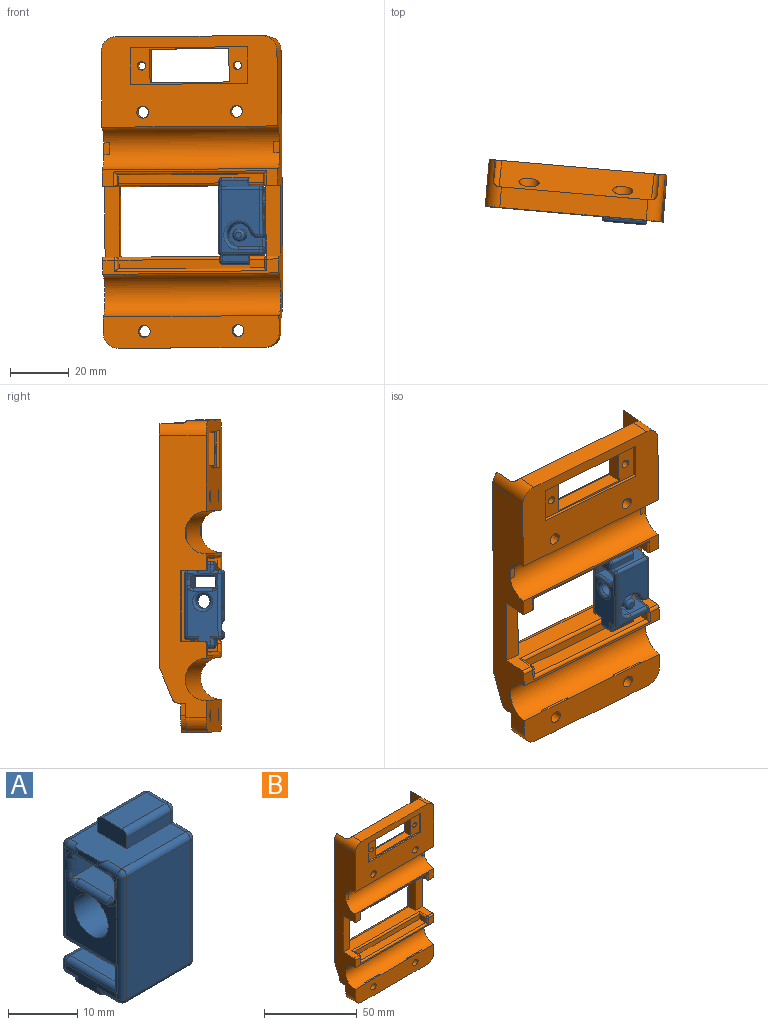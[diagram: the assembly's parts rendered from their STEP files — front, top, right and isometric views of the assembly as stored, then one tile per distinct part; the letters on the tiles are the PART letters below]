
ASSEMBLY  parts=2 mates=1
PART A: 97 faces, bbox 15.1x12.6x29.6 mm
  f0: cylinder r=2.45mm len=9mm, axis (1,0,0), area 131.3mm2, adj f77,f94,f95
  f1: plane 10.5x1.92mm, normal (-1,0,0), area 13.7mm2, adj f2,f24,f39,f40,f42,f43,f44,f92
  f2: cylinder r=1mm len=1mm, axis (0,0,-1), area 1.5mm2, adj f1,f25,f38,f91
  f3: torus R=2mm, axis (-1,0,0), area 2.6mm2, adj f8,f36,f43,f67,f68
  f4: torus R=2mm, axis (-1,0,0), area 2.6mm2, adj f7,f36,f37,f67,f70
  f5: torus R=2mm, axis (-1,0,0), area 2.6mm2, adj f12,f48,f63,f67,f68
  f6: torus R=2mm, axis (-1,0,0), area 2.6mm2, adj f11,f47,f48,f67,f70
  f7: plane 2x2mm, normal (-1,0,0), area 0.9mm2, adj f4,f36,f37
  f8: plane 2x2mm, normal (-1,0,0), area 0.9mm2, adj f3,f36,f43
  f9: plane 11.58x10.5mm, normal (-1,0,0), area 64.9mm2, adj f37,f43,f71,f72,f73,f88,f96
  f10: plane 20.5x10.5mm, normal (1,0,0), area 139.1mm2, adj f47,f51,f53,f57,f60,f62,f63,f74
  f11: plane 2x2mm, normal (1,0,0), area 0.9mm2, adj f6,f47,f48
  f12: plane 2x2mm, normal (1,0,0), area 0.9mm2, adj f5,f48,f63
  f13: plane 4x1mm, normal (-1,0,0), area 4mm2, adj f21,f22,f28,f36
  f14: plane 4x3mm, normal (1,0,0), area 12mm2, adj f48,f50,f54,f58
  f15: plane 9x2mm, normal (0,1,0), area 18mm2, adj f20,f24,f53,f65
  f16: plane 9x2mm, normal (0,1,0), area 18mm2, adj f28,f32,f50,f66
  f17: plane 9x2mm, normal (0,-1,0), area 18mm2, adj f19,f24,f60,f65
  f18: plane 9x4mm, normal (0,0,-1), area 36mm2, adj f19,f20,f57,f65
  f19: cylinder r=1mm len=9mm, axis (-1,0,0), area 14.1mm2, adj f17,f18,f59,f65
  f20: cylinder r=1mm len=9mm, axis (1,0,0), area 14.1mm2, adj f15,f18,f55,f65
  f21: cylinder r=1mm len=1mm, axis (0,0,-1), area 0.6mm2, adj f13,f28,f36
  f22: cylinder r=1mm len=1mm, axis (0,0,1), area 0.6mm2, adj f13,f28,f36
  f23: plane 21.5x13mm, normal (0,-1,0), area 279.5mm2, adj f29,f34,f43,f63
  f24: plane 14x10.5mm, normal (0,0,-1), area 88.1mm2, adj f1,f15,f17,f29,f30,f39,f40,f42
  f25: plane 21.5x13mm, normal (0,1,0), area 183.9mm2, adj f2,f30,f31,f37,f47,f84,f85,f87
  f26: plane 9x4mm, normal (0,0,1), area 36mm2, adj f32,f33,f54,f66
  f27: plane 9x2mm, normal (0,-1,0), area 18mm2, adj f28,f33,f58,f66
  f28: plane 14x10.5mm, normal (0,0,1), area 88.1mm2, adj f13,f16,f21,f22,f27,f31,f34,f36
  f29: cylinder r=1mm len=13mm, axis (1,0,0), area 20.4mm2, adj f23,f24,f45,f64
  f30: cylinder r=1mm len=13mm, axis (-1,0,0), area 20.4mm2, adj f24,f25,f38,f49
  f31: cylinder r=1mm len=13mm, axis (1,0,0), area 20.4mm2, adj f25,f28,f35,f46
  f32: cylinder r=1mm len=9mm, axis (1,0,0), area 14.1mm2, adj f16,f26,f52,f66
  f33: cylinder r=1mm len=9mm, axis (-1,0,0), area 14.1mm2, adj f26,f27,f56,f66
  f34: cylinder r=1mm len=13mm, axis (-1,0,0), area 20.4mm2, adj f23,f28,f41,f61
  f35: sphere r=1mm, area 1.6mm2, adj f31,f36,f37
  f36: cylinder r=1mm len=10.5mm, axis (0,1,0), area 18.4mm2, adj f3,f4,f7,f8,f13,f21,f22,f28
  f37: cylinder r=1mm len=15.58mm, axis (0,0,-1), area 27.6mm2, adj f4,f7,f9,f25,f35,f70,f73,f86
  f38: sphere r=1mm, area 1.6mm2, adj f2,f30,f39
  f39: cylinder r=1mm len=2.5mm, axis (0,-1,0), area 2.9mm2, adj f1,f24,f38,f40
  f40: cylinder r=1mm len=1mm, axis (0,0,-1), area 0.6mm2, adj f1,f24,f39
  f41: sphere r=1mm, area 1.6mm2, adj f34,f36,f43
  f42: cylinder r=1mm len=1mm, axis (0,0,1), area 0.6mm2, adj f1,f24,f44
  f43: cylinder r=1mm len=21.5mm, axis (0,0,1), area 36.9mm2, adj f1,f3,f8,f9,f23,f41,f45,f68
  f44: cylinder r=1mm len=4mm, axis (0,-1,0), area 5.3mm2, adj f1,f24,f42,f45
  f45: sphere r=1mm, area 1.6mm2, adj f29,f43,f44
  f46: sphere r=1mm, area 1.6mm2, adj f31,f47,f48
  f47: cylinder r=1mm len=21.5mm, axis (0,0,1), area 36.9mm2, adj f6,f10,f11,f25,f46,f49,f70,f75
  f48: cylinder r=1mm len=10.5mm, axis (0,-1,0), area 18.4mm2, adj f5,f6,f11,f12,f14,f28,f46,f50
  f49: sphere r=1mm, area 1.6mm2, adj f30,f47,f51
  f50: cylinder r=1mm len=3mm, axis (0,0,1), area 3.7mm2, adj f14,f16,f48,f52
  f51: cylinder r=1mm len=2.5mm, axis (0,1,0), area 2.9mm2, adj f10,f24,f49,f53
  f52: sphere r=1mm, area 1.6mm2, adj f32,f50,f54
  f53: cylinder r=1mm len=3mm, axis (0,0,1), area 3.7mm2, adj f10,f15,f51,f55
  f54: cylinder r=1mm len=4mm, axis (0,-1,0), area 6.3mm2, adj f14,f26,f52,f56
  f55: sphere r=1mm, area 1.6mm2, adj f20,f53,f57
  f56: sphere r=1mm, area 1.6mm2, adj f33,f54,f58
  f57: cylinder r=1mm len=4mm, axis (0,1,0), area 6.3mm2, adj f10,f18,f55,f59
  f58: cylinder r=1mm len=3mm, axis (0,0,-1), area 3.7mm2, adj f14,f27,f48,f56
  f59: sphere r=1mm, area 1.6mm2, adj f19,f57,f60
  f60: cylinder r=1mm len=3mm, axis (0,0,-1), area 3.7mm2, adj f10,f17,f59,f62
  f61: sphere r=1mm, area 1.6mm2, adj f34,f48,f63
  f62: cylinder r=1mm len=4mm, axis (0,1,0), area 5.3mm2, adj f10,f24,f60,f64
  f63: cylinder r=1mm len=21.5mm, axis (0,0,-1), area 36.9mm2, adj f5,f10,f12,f23,f61,f64,f68,f74
  f64: sphere r=1mm, area 1.6mm2, adj f29,f62,f63
  f65: plane 6x3mm, normal (-1,0,0), area 17.6mm2, adj f15,f17,f18,f19,f20,f24
  f66: plane 6x3mm, normal (-1,0,0), area 17.6mm2, adj f16,f26,f27,f28,f32,f33
  f67: plane 14.73x8.61mm, normal (0,0,-1), area 112.3mm2, adj f3,f4,f5,f6,f36,f48,f68,f70
  f68: plane 14.73x4.11mm, normal (0,1,0), area 53.8mm2, adj f3,f5,f43,f63,f67,f69,f72,f74
  f69: plane 14.73x8.61mm, normal (0,0,1), area 112.3mm2, adj f68,f70,f71,f72,f73,f74,f75,f76
  f70: plane 14.73x4.11mm, normal (0,-1,0), area 53.8mm2, adj f4,f6,f37,f47,f67,f69,f73,f75
  f71: cylinder r=1mm len=6.5mm, axis (0,-1,0), area 10.2mm2, adj f9,f69,f72,f73
  f72: torus R=2mm, axis (-1,0,0), area 2.6mm2, adj f9,f43,f68,f69,f71
  f73: torus R=2mm, axis (-1,0,0), area 2.6mm2, adj f9,f37,f69,f70,f71
  f74: torus R=2mm, axis (-1,0,0), area 2.6mm2, adj f10,f63,f68,f69,f76
  f75: torus R=2mm, axis (-1,0,0), area 2.6mm2, adj f10,f47,f69,f70,f76
  f76: cylinder r=1mm len=6.5mm, axis (0,1,0), area 10.2mm2, adj f10,f69,f74,f75
  f77: cylinder r=4mm len=9.52mm, axis (0,-1,0), area 161.2mm2, adj f0,f78,f79,f82,f87
  f78: cylinder r=3mm len=9.52mm, axis (0,-1,0), area 36.6mm2, adj f77,f81,f82,f85
  f79: plane 9.52x7.23mm, normal (0,0,1), area 68.8mm2, adj f77,f82,f89,f92
  f80: cylinder r=2mm len=9.52mm, axis (0,-1,0), area 119.6mm2, adj f82,f93
  f81: plane 9.52x0.52mm, normal (0,0,-1), area 4.9mm2, adj f78,f82,f84,f88
  f82: plane 11.23x8mm, normal (0,1,0), area 52.1mm2, adj f77,f78,f79,f80,f81,f90
  f83: plane 2x2mm, normal (0,1,0), area 3.1mm2, adj f93
  f84: cylinder r=1mm len=1mm, axis (1,0,0), area 0.8mm2, adj f25,f81,f85,f86
  f85: torus R=2mm, axis (0,1,0), area 5.3mm2, adj f25,f78,f84,f87
  f86: sphere r=1mm, area 1.6mm2, adj f37,f84,f88
  f87: torus R=5mm, axis (0,1,0), area 30.3mm2, adj f25,f77,f85,f89
  f88: cylinder r=1mm len=10.51mm, axis (0,1,0), area 15.5mm2, adj f9,f43,f81,f86,f90
  f89: cylinder r=1mm len=7.23mm, axis (-1,0,0), area 11.4mm2, adj f25,f79,f87,f91
  f90: cylinder r=1mm len=4.98mm, axis (0,0,1), area 5.8mm2, adj f43,f82,f88,f92
  f91: sphere r=1mm, area 1.6mm2, adj f2,f89,f92
  f92: cylinder r=1mm len=10.51mm, axis (0,-1,0), area 15.5mm2, adj f1,f43,f79,f90,f91
  f93: torus R=1mm, axis (0,1,0), area 16.2mm2, adj f80,f83
  f94: torus R=3.45mm, axis (-1,0,0), area 27.8mm2, adj f0,f10
  f95: plane 6.9x6.9mm, normal (-1,0,0), area 18.5mm2, adj f0,f96
  f96: cylinder r=3.45mm len=6.9mm, axis (-1,0,0), area 108.4mm2, adj f9,f95
PART B: 116 faces, bbox 60.6x18.4x106.6 mm
  f0: plane 8.62x7mm, normal (0,0,-1), area 60.3mm2, adj f2,f19,f105,f112
  f1: plane 31.24x7mm, normal (0,0,-1), area 218.7mm2, adj f18,f19,f101,f105
  f2: plane 13.62x10mm, normal (0,1,0), area 84.1mm2, adj f0,f5,f30,f105,f107,f112
  f3: plane 13.62x10mm, normal (0,1,0), area 84.1mm2, adj f5,f26,f29,f100,f101,f114
  f4: cylinder r=7.25mm len=60mm, axis (1,0,0), area 1347.8mm2, adj f19,f25,f29,f30,f102,f103,f104,f109
  f5: plane 60x2.75mm, normal (0,0,-1), area 107mm2, adj f2,f3,f18,f29,f30,f96,f98,f99
  f6: plane 24x5mm, normal (1,0,0), area 120mm2, adj f16,f22,f24,f90
  f7: plane 5x3mm, normal (-1,0,0), area 15mm2, adj f44,f71,f73,f75
  f8: plane 5x3mm, normal (1,0,0), area 15mm2, adj f43,f70,f81,f86
  f9: plane 24x5mm, normal (-1,0,0), area 120mm2, adj f22,f23,f24,f89
  f10: plane 60.59x22.59mm, normal (0,0.93,0.38), area 1157mm2, adj f11,f17,f29,f30,f39,f41,f63,f68
  f11: plane 52x20mm, normal (0,1,0), area 539.9mm2, adj f10,f28,f51,f52,f53,f54,f92,f94
  f12: plane 40x12.5mm, normal (0,-1,0), area 181.4mm2, adj f13,f14,f47,f48,f49,f50,f56,f57
  f13: cylinder r=1.4mm len=4.8mm, axis (0,-1,0), area 42.2mm2, adj f12,f55
  f14: cylinder r=1.4mm len=4.8mm, axis (0,-1,0), area 42.2mm2, adj f12,f55
  f15: plane 60x30.75mm, normal (0,-1,0), area 1309.1mm2, adj f20,f28,f29,f30,f31,f32,f47,f48
  f16: plane 24x5mm, normal (0,-1,0), area 120mm2, adj f6,f22,f24,f29
  f17: plane 60x41.61mm, normal (0,1,0), area 984.4mm2, adj f10,f29,f30,f88,f89,f90,f91,f97
  f18: plane 31.24x10mm, normal (0,1,0), area 219.1mm2, adj f1,f5,f99,f101,f105,f106
  f19: plane 60x10.81mm, normal (0,-1,0), area 610.2mm2, adj f0,f1,f4,f26,f29,f30,f33,f34
  f20: cylinder r=7.25mm len=60mm, axis (1,0,0), area 1351.3mm2, adj f15,f21,f29,f30,f60,f61,f65,f66
  f21: plane 60x5.75mm, normal (0,-1,0), area 85mm2, adj f20,f22,f29,f30,f72,f73,f74
  f22: plane 60x14mm, normal (0,0,-1), area 426mm2, adj f6,f9,f16,f21,f23,f29,f30,f75
  f23: plane 24x5mm, normal (0,-1,0), area 120mm2, adj f9,f22,f24,f30
  f24: plane 60x13mm, normal (0,0,1), area 418mm2, adj f6,f9,f16,f23,f29,f30,f79,f82
  f25: plane 60x4.75mm, normal (0,-1,0), area 77mm2, adj f4,f29,f30,f78,f79,f80,f81,f82
  f26: plane 8.62x7mm, normal (0,0,-1), area 60.3mm2, adj f3,f19,f101,f114
  f27: plane 60x10.39mm, normal (0,0.93,-0.38), area 673.8mm2, adj f29,f30,f96,f97
  f28: plane 50x7mm, normal (0,0,1), area 350mm2, adj f11,f15,f113,f115
  f29: plane 96x16mm, normal (-1,0,0), area 1080.5mm2, adj f3,f4,f5,f10,f15,f16,f17,f19
  f30: plane 96x16mm, normal (1,0,0), area 1080.5mm2, adj f2,f4,f5,f10,f15,f17,f19,f20
  f31: cylinder r=2mm len=5mm, axis (0,-1,0), area 62.8mm2, adj f15,f42
  f32: cylinder r=2mm len=5mm, axis (0,-1,0), area 62.8mm2, adj f15,f40
  f33: cylinder r=2mm len=5mm, axis (0,-1,0), area 62.8mm2, adj f19,f38
  f34: cylinder r=2mm len=5mm, axis (0,-1,0), area 62.8mm2, adj f19,f36
  f35: cylinder r=3.45mm len=6.9mm, axis (0,-1,0), area 98mm2, adj f36,f108
  f36: plane 6.9x6.9mm, normal (0,1,0), area 24.8mm2, adj f34,f35
  f37: cylinder r=3.45mm len=6.9mm, axis (0,-1,0), area 98mm2, adj f38,f98
  f38: plane 6.9x6.9mm, normal (0,1,0), area 24.8mm2, adj f33,f37
  f39: cylinder r=3.45mm len=6.9mm, axis (0,-1,0), area 94.3mm2, adj f10,f40
  f40: plane 6.9x6.9mm, normal (0,1,0), area 24.8mm2, adj f32,f39
  f41: cylinder r=3.45mm len=6.9mm, axis (0,-1,0), area 94.3mm2, adj f10,f42
  f42: plane 6.9x6.9mm, normal (0,1,0), area 24.8mm2, adj f31,f41
  f43: plane 50x5mm, normal (0,0,1), area 250mm2, adj f8,f45,f70,f78
  f44: plane 50x5mm, normal (0,0,-1), area 250mm2, adj f7,f46,f71,f72
  f45: plane 5x3mm, normal (-1,0,0), area 15mm2, adj f43,f70,f80,f85
  f46: plane 5x3mm, normal (1,0,0), area 15mm2, adj f44,f71,f74,f76
  f47: plane 40x1mm, normal (0,0,-1), area 40mm2, adj f12,f15,f48,f50
  f48: plane 12.5x1mm, normal (1,0,0), area 12.5mm2, adj f12,f15,f47,f49
  f49: plane 40x1mm, normal (0,0,1), area 40mm2, adj f12,f15,f48,f50
  f50: plane 12.5x1mm, normal (-1,0,0), area 12.5mm2, adj f12,f15,f47,f49
  f51: plane 40x1.2mm, normal (0,0,-1), area 48mm2, adj f11,f52,f54,f55
  f52: plane 12.5x1.2mm, normal (-1,0,0), area 15mm2, adj f11,f51,f53,f55
  f53: plane 40x1.2mm, normal (0,0,1), area 48mm2, adj f11,f52,f54,f55
  f54: plane 12.5x1.2mm, normal (1,0,0), area 15mm2, adj f11,f51,f53,f55
  f55: plane 40x12.5mm, normal (0,1,0), area 181.4mm2, adj f13,f14,f51,f52,f53,f54,f56,f57
  f56: plane 11.35x4.8mm, normal (1,0,0), area 54.5mm2, adj f12,f55,f57,f59
  f57: plane 27x4.8mm, normal (0,0,-1), area 129.6mm2, adj f12,f55,f56,f58
  f58: plane 11.35x4.8mm, normal (-1,0,0), area 54.5mm2, adj f12,f55,f57,f59
  f59: plane 27x4.8mm, normal (0,0,1), area 129.6mm2, adj f12,f55,f56,f58
  f60: plane 3.78x0.25mm, normal (1,0,0), area 0.6mm2, adj f20,f61
  f61: plane 3.78x2mm, normal (0,-1,0), area 7.5mm2, adj f20,f29,f60
  f62: plane 35.72x7mm, normal (1,0,0), area 190.1mm2, adj f64,f94,f95,f115
  f63: plane 4.02x0.1mm, normal (0,0,-1), area 0.3mm2, adj f10,f29,f64,f95
  f64: plane 40.8x3.46mm, normal (0,1,0), area 81.1mm2, adj f29,f62,f63,f95,f115
  f65: plane 3.78x2mm, normal (0,-1,0), area 7.5mm2, adj f20,f30,f66
  f66: plane 3.78x0.25mm, normal (-1,0,0), area 0.6mm2, adj f20,f65
  f67: plane 35.72x7mm, normal (-1,0,0), area 190.1mm2, adj f69,f92,f93,f113
  f68: plane 4.02x0.1mm, normal (0,0,-1), area 0.3mm2, adj f10,f30,f69,f93
  f69: plane 40.8x3.46mm, normal (0,1,0), area 81.1mm2, adj f30,f67,f68,f93,f113
  f70: plane 50x3mm, normal (0,-1,0), area 150mm2, adj f8,f43,f45,f87
  f71: plane 50x3mm, normal (0,-1,0), area 150mm2, adj f7,f44,f46,f77
  f72: cylinder r=1mm len=52mm, axis (1,0,0), area 80.1mm2, adj f21,f44,f73,f74
  f73: cylinder r=1mm len=5mm, axis (0,0,-1), area 6.3mm2, adj f7,f21,f72,f75
  f74: cylinder r=1mm len=5mm, axis (0,0,1), area 6.3mm2, adj f21,f46,f72,f76
  f75: cylinder r=1mm len=7mm, axis (0,1,0), area 9.4mm2, adj f7,f22,f73,f77
  f76: cylinder r=1mm len=7mm, axis (0,-1,0), area 9.4mm2, adj f22,f46,f74,f77
  f77: cylinder r=1mm len=52mm, axis (1,0,0), area 80.1mm2, adj f22,f71,f75,f76
  f78: cylinder r=1mm len=52mm, axis (-1,0,0), area 80.1mm2, adj f25,f43,f80,f81
  f79: cylinder r=1mm len=4mm, axis (1,0,0), area 6.3mm2, adj f24,f25,f30,f83
  f80: cylinder r=1mm len=4mm, axis (0,0,-1), area 5.5mm2, adj f25,f45,f78,f83
  f81: cylinder r=1mm len=4mm, axis (0,0,1), area 5.5mm2, adj f8,f25,f78,f84
  f82: cylinder r=1mm len=4mm, axis (1,0,0), area 6.3mm2, adj f24,f25,f29,f84
  f83: sphere r=1mm, area 1.6mm2, adj f79,f80,f85
  f84: sphere r=1mm, area 1.6mm2, adj f81,f82,f86
  f85: cylinder r=1mm len=6mm, axis (0,-1,0), area 8.6mm2, adj f24,f45,f83,f87
  f86: cylinder r=1mm len=6mm, axis (0,1,0), area 8.6mm2, adj f8,f24,f84,f87
  f87: cylinder r=1mm len=52mm, axis (1,0,0), area 80.1mm2, adj f24,f70,f85,f86
  f88: cylinder r=2mm len=54mm, axis (-1,0,0), area 161.6mm2, adj f17,f24,f89,f90
  f89: cylinder r=2mm len=28mm, axis (0,0,-1), area 80mm2, adj f9,f17,f88,f91
  f90: cylinder r=2mm len=28mm, axis (0,0,1), area 80mm2, adj f6,f17,f88,f91
  f91: cylinder r=2mm len=54mm, axis (1,0,0), area 161.6mm2, adj f17,f22,f89,f90
  f92: cylinder r=2mm len=19.9mm, axis (0,0,1), area 60.5mm2, adj f11,f67,f93,f113
  f93: cylinder r=2mm len=22.59mm, axis (0,0.38,-0.93), area 68.4mm2, adj f10,f67,f68,f69,f92
  f94: cylinder r=2mm len=19.9mm, axis (0,0,-1), area 60.5mm2, adj f11,f62,f95,f115
  f95: cylinder r=2mm len=22.59mm, axis (0,-0.38,0.93), area 68.4mm2, adj f10,f62,f63,f64,f94
  f96: cylinder r=2mm len=60mm, axis (1,0,0), area 141.9mm2, adj f5,f27,f29,f30
  f97: cylinder r=2mm len=60mm, axis (-1,0,0), area 46.6mm2, adj f17,f27,f29,f30
  f98: plane 11.53x10.01mm, normal (0,1,0), area 63.7mm2, adj f5,f37,f99,f100,f101
  f99: plane 4.19x2.52mm, normal (1,0,0.01), area 10.6mm2, adj f5,f18,f98,f101
  f100: plane 4.25x2.52mm, normal (-1,0,0), area 10.7mm2, adj f3,f5,f98,f101
  f101: cylinder r=5.76mm len=11.53mm, axis (0,-1,0), area 51.1mm2, adj f1,f3,f18,f19,f26,f98,f99,f100
  f102: plane 0.82x0.05mm, normal (-1,0,0), area 0mm2, adj f4,f19,f104
  f103: plane 0.82x0.05mm, normal (1,0,0.01), area 0mm2, adj f4,f19,f104
  f104: plane 11.47x0.82mm, normal (0,0,1), area 9.4mm2, adj f4,f19,f102,f103
  f105: cylinder r=5.76mm len=11.53mm, axis (0,-1,0), area 51.1mm2, adj f0,f1,f2,f18,f19,f106,f107,f108
  f106: plane 4.19x2.52mm, normal (-1,0,0.01), area 10.6mm2, adj f5,f18,f105,f108
  f107: plane 4.25x2.52mm, normal (1,0,0), area 10.7mm2, adj f2,f5,f105,f108
  f108: plane 11.53x10.01mm, normal (0,1,0), area 63.7mm2, adj f5,f35,f105,f106,f107
  f109: plane 0.82x0.05mm, normal (1,0,0), area 0mm2, adj f4,f19,f111
  f110: plane 0.82x0.05mm, normal (-1,0,0.01), area 0mm2, adj f4,f19,f111
  f111: plane 11.47x0.82mm, normal (0,0,1), area 9.4mm2, adj f4,f19,f109,f110
  f112: cylinder r=5mm len=7mm, axis (0,1,0), area 55mm2, adj f0,f2,f19,f30
  f113: cylinder r=5mm len=16mm, axis (0,-1,0), area 97.7mm2, adj f11,f15,f28,f30,f67,f69,f92
  f114: cylinder r=5mm len=7mm, axis (0,-1,0), area 55mm2, adj f3,f19,f26,f29
  f115: cylinder r=5mm len=16mm, axis (0,1,0), area 97.7mm2, adj f11,f15,f28,f29,f62,f64,f94
PLACE A rot(axis=(0,0,1),175deg) t=(-21.48,-18.91,6.02)mm
PLACE B rot(axis=(0,-0.09,-1),5deg) t=(18.27,-27.14,6.29)mm
MATE parallel B.f70 <-> A.f17  axis (-0.09,-1,0) through (-10.99,-18.57,-6.93)mm
